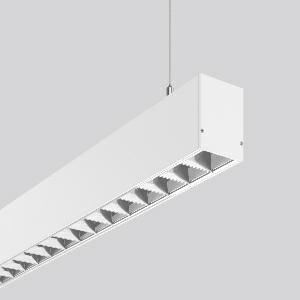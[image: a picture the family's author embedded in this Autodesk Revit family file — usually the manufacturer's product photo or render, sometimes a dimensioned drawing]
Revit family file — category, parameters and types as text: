
# Revit family: less_is_more_50_312339_002_76_f044
name_source: partatom
category: Lighting Fixtures
units: mm (PartAtom-declared; Revit-internal decimal feet)

## family parameters
Cut with Voids When Loaded = No
Host = Face
Light Source = No
Part Type = Normal
Room Calculation Point = No
Round Connector Dimension = Use Diameter
Shared = No

## types (1)
- LESS IS MORE 50 (1 x LED Modul 830, 5900 lm, 3000)
    Apparent Load = 48 VA
    CIE Flux Codes = 95 100 100 100 100
    Color Rendering = 80
    Color Temperature = 3000
    Default Elevation = 1800 mm
    Description = Series: LESS IS MORE 50
Linear pendant luminaire for aesthetically sophisticated lighting. Housing: extruded aluminium profile, powder-coated. End cap aluminium powder-coated. Canopy made of aluminium, powder-coated. Alea optical system: Reflector structure (ABS, Aluminium-coated, highly polished) with integrated diffuser made of non-yellowing plastic (PMMA) opal for glare-free light at the workstation (screen-compliant according to EN 12464-1). Direct light emission. Suitable for pendant. 2-point steel cable suspension freely positionable and infinitely height-adjustable. Special lengths available on request. LED unit with integrated converter interchangeable and removable. Suitable for through-wiring. With sensors or as a safety luminaire on request. 
Colour: traffic white, matt (RAL 9016)
Length: 1967 mm
Width: 57 mm
Height: 75 mm
Suspension length: 2000 mm
Lamp: LED
Socket: without socket
Colour temperature: 3000K
Colour rendering index (CRI): 80
System power: 48 W
Rated luminous flux: 5900 lm
Luminous efficiency: 123 lm/W
Control gear: Converter, dimmable, DALI
Protection class: I
Type of protection: IP 20
    Height = 75 mm
    Lamp = 1 x LED Modul 830
    Lamp Light Flux = 5900 lm
    Lamp count = 1
    Length = 1967 mm
    Lifetime = 50000 h
    Luminous efficacy = 123 lm/W
    Manufacturer = RZB
    ModVariant = No
    Model = 312339.002.76
    Mounting Place = Ceiling
    Mounting Type = Pendant
    Number of Poles = 1
    OnlyDefault = Yes
    Power Factor = 1
    Product Name = LESS IS MORE 50
    Product group = Pendant LED linear luminaires
    ProductGroupID = 907
    Protection Class = Protection class I
    Protection Degree = IP 20
    RLX_Detail_Level = 1
    RLX_Emergency_Light_Flux = 0 lm
    RLX_Emergency_Type = 0
    RLX_Emergency_Type_DB = No
    RlxData = <blob elided: 33133 chars, md5=632d987a>
    Socket = socket
    Standby Power = 0 W
    System Light Flux = 5900 lm
    System Power = 48 W
    Type Comments = Product without accessories
    Type Image = 312342.002.jpg
    URL = http://relux.com
    VarID = ---
    Voltage = 230 V
    Voltage Range = 220-240 V
    Weight = 0.00 kg
    Width = 57 mm

## geometry (parser evidence)
native form markers: Blend x4, Sweep x12
no freeform markers — native parametric forms only
